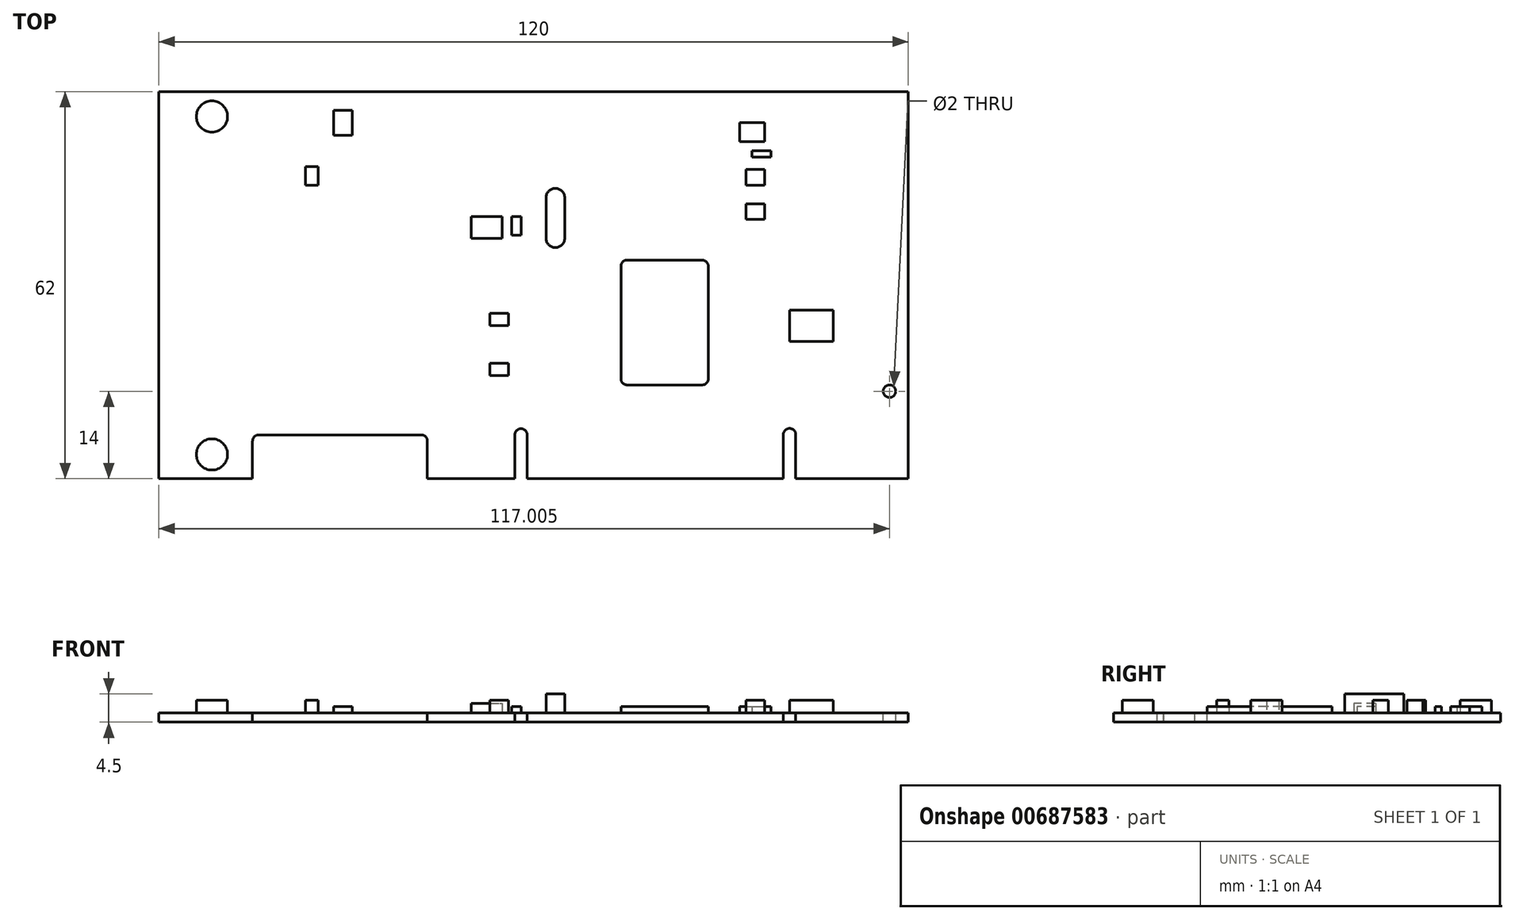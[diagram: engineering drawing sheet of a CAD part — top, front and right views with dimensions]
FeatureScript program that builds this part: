
annotation { "Feature Type Name" : "Feature", "Feature Type Description" : "" }
export const myFeature = defineFeature(function(context is Context, id is Id, definition is map)
    precondition{}
    {
        {
            var Q0;
            Q0=qCreatedBy(makeId("Top.planeOp"),FACE);
            var sketch = newSketch(context, id + "F0", { "sketchPlane" : qUnion([Q0])});
            skLineSegment(sketch, "E0.bottom", {"start": v(-77.62, 37.41) * mm, "end": v(42.38, 37.41) * mm});
            skLineSegment(sketch, "E0.top", {"start": v(-77.62, -24.59) * mm, "end": v(42.38, -24.59) * mm});
            skLineSegment(sketch, "E0.left", {"start": v(-77.62, 37.41) * mm, "end": v(-77.62, -24.59) * mm});
            skLineSegment(sketch, "E0.right", {"start": v(42.38, 37.41) * mm, "end": v(42.38, -24.59) * mm});
            skSolve(sketch);
        }
        {
            var Q0;
            Q0 = qSketchRegion(id + "F0", true);
            extrude(context, id + "F1", {"entities" : qUnion([Q0]), "depth" : 1.5 * mm, "offsetDistance" : 25 * mm});
        }
        {
            var Q0;
            Q0=makeQuery(id+"F1.opExtrude","CAP_FACE",FACE,{"disambiguationData":[OSD([sQuery(id+"F0.wireOp",EDGE,"E0.bottom"),sQuery(id+"F0.wireOp",EDGE,"E0.top"),sQuery(id+"F0.wireOp",EDGE,"E0.left"),sQuery(id+"F0.wireOp",EDGE,"E0.right")])],"isStart":false});
            var sketch = newSketch(context, id + "F2", { "sketchPlane" : qUnion([Q0])});
            skLineSegment(sketch, "E1", {"start": v(-77.62, -24.59) * mm, "end": v(-62.62, -24.59) * mm});
            skLineSegment(sketch, "E2", {"start": v(-62.62, -24.59) * mm, "end": v(-34.62, -24.59) * mm});
            skLineSegment(sketch, "E3.top", {"start": v(-61.62, -17.59) * mm, "end": v(-35.62, -17.59) * mm});
            skLineSegment(sketch, "E3.left", {"start": v(-62.62, -24.59) * mm, "end": v(-62.62, -18.59) * mm});
            skLineSegment(sketch, "E3.right", {"start": v(-34.62, -24.59) * mm, "end": v(-34.62, -18.59) * mm});
            skPoint(sketch, "E4.visualSharp", {"position": v(-62.62, -17.59) * mm});
            skArc(sketch, "E4.filletArc", {"start": v(-61.62, -17.59) * mm, "mid": v(-62.32, -17.88) * mm, "end": v(-62.62, -18.59) * mm});
            skPoint(sketch, "E5.visualSharp", {"position": v(-34.62, -17.59) * mm});
            skArc(sketch, "E5.filletArc", {"start": v(-34.62, -18.59) * mm, "mid": v(-34.9, -17.88) * mm, "end": v(-35.62, -17.59) * mm});
            skSolve(sketch);
        }
        {
            var Q0;
            Q0 = qSketchRegion(id + "F2", true);
            extrude(context, id + "F3", {"entities" : qUnion([Q0]), "operationType" : NewBodyOperationType.REMOVE, "endBound" : BoundingType.THROUGH_ALL, "oppositeDirection" : true, "depth" : 25 * mm, "offsetDistance" : 25 * mm});
        }
        {
            var Q0;
            Q0=makeQuery(id+"F1.opExtrude","CAP_FACE",FACE,{"disambiguationData":[OSD([sQuery(id+"F0.wireOp",EDGE,"E0.bottom"),sQuery(id+"F0.wireOp",EDGE,"E0.top"),sQuery(id+"F0.wireOp",EDGE,"E0.left"),sQuery(id+"F0.wireOp",EDGE,"E0.right")])],"isStart":false});
            var sketch = newSketch(context, id + "F4", { "sketchPlane" : qUnion([Q0])});
            skLineSegment(sketch, "E6", {"start": v(-34.62, -24.59) * mm, "end": v(-20.62, -24.59) * mm});
            skLineSegment(sketch, "E7", {"start": v(-20.62, -24.59) * mm, "end": v(-20.62, -17.59) * mm});
            skLineSegment(sketch, "E8", {"start": v(-18.62, -24.59) * mm, "end": v(-18.62, -17.59) * mm});
            skArc(sketch, "E9", {"start": v(-18.62, -17.59) * mm, "mid": v(-19.62, -16.59) * mm, "end": v(-20.62, -17.59) * mm});
            skPoint(sketch, "E10.orphan", {"position": v(-20.62, -16.59) * mm});
            skPoint(sketch, "E11.orphan", {"position": v(-18.62, -16.59) * mm});
            skLineSegment(sketch, "E12", {"start": v(-20.62, -24.59) * mm, "end": v(-18.62, -24.59) * mm});
            skSolve(sketch);
        }
        {
            var Q0;
            Q0 = qSketchRegion(id + "F4", true);
            extrude(context, id + "F5", {"entities" : qUnion([Q0]), "operationType" : NewBodyOperationType.REMOVE, "endBound" : BoundingType.THROUGH_ALL, "oppositeDirection" : true, "depth" : 25 * mm, "offsetDistance" : 25 * mm});
        }
        {
            var Q0;
            Q0=makeQuery(id+"F1.opExtrude","CAP_FACE",FACE,{"disambiguationData":[OSD([sQuery(id+"F0.wireOp",EDGE,"E0.bottom"),sQuery(id+"F0.wireOp",EDGE,"E0.top"),sQuery(id+"F0.wireOp",EDGE,"E0.left"),sQuery(id+"F0.wireOp",EDGE,"E0.right")])],"isStart":false});
            var sketch = newSketch(context, id + "F6", { "sketchPlane" : qUnion([Q0])});
            skLineSegment(sketch, "E13", {"start": v(-18.62, -24.59) * mm, "end": v(22.38, -24.59) * mm});
            skLineSegment(sketch, "E14", {"start": v(22.38, -24.59) * mm, "end": v(22.38, -17.54) * mm});
            skLineSegment(sketch, "E15", {"start": v(24.38, -24.59) * mm, "end": v(24.38, -17.54) * mm});
            skArc(sketch, "E16", {"start": v(24.38, -17.54) * mm, "mid": v(23.38, -16.54) * mm, "end": v(22.38, -17.54) * mm});
            skPoint(sketch, "E17.orphan", {"position": v(22.38, -16.59) * mm});
            skPoint(sketch, "E18.orphan", {"position": v(24.38, -16.59) * mm});
            skLineSegment(sketch, "E19", {"start": v(22.38, -24.59) * mm, "end": v(24.38, -24.59) * mm});
            skSolve(sketch);
        }
        {
            var Q0;
            Q0 = qSketchRegion(id + "F6", true);
            extrude(context, id + "F7", {"entities" : qUnion([Q0]), "operationType" : NewBodyOperationType.REMOVE, "endBound" : BoundingType.THROUGH_ALL, "oppositeDirection" : true, "depth" : 25 * mm, "offsetDistance" : 25 * mm});
        }
        {
            var Q0;
            Q0=makeQuery(id+"F1.opExtrude","CAP_FACE",FACE,{"disambiguationData":[OSD([sQuery(id+"F0.wireOp",EDGE,"E0.bottom"),sQuery(id+"F0.wireOp",EDGE,"E0.top"),sQuery(id+"F0.wireOp",EDGE,"E0.left"),sQuery(id+"F0.wireOp",EDGE,"E0.right")])],"isStart":false});
            var sketch = newSketch(context, id + "F8", { "sketchPlane" : qUnion([Q0])});
            skCircle(sketch, "E20", {"center": v(39.38, -10.59) * mm, "radius": 1 * mm});
            skSolve(sketch);
        }
        {
            var Q0;
            Q0 = qSketchRegion(id + "F8", true);
            extrude(context, id + "F9", {"entities" : qUnion([Q0]), "operationType" : NewBodyOperationType.REMOVE, "endBound" : BoundingType.THROUGH_ALL, "oppositeDirection" : true, "depth" : 25 * mm, "offsetDistance" : 25 * mm});
        }
        {
            var Q0;
            Q0=makeQuery(id+"F1.opExtrude","CAP_FACE",FACE,{"disambiguationData":[OSD([sQuery(id+"F0.wireOp",EDGE,"E0.bottom"),sQuery(id+"F0.wireOp",EDGE,"E0.top"),sQuery(id+"F0.wireOp",EDGE,"E0.left"),sQuery(id+"F0.wireOp",EDGE,"E0.right")])],"isStart":false});
            var sketch = newSketch(context, id + "F10", { "sketchPlane" : qUnion([Q0])});
            skLineSegment(sketch, "E21.bottom", {"start": v(23.38, 2.41) * mm, "end": v(30.38, 2.41) * mm});
            skLineSegment(sketch, "E21.top", {"start": v(23.38, -2.59) * mm, "end": v(30.38, -2.59) * mm});
            skLineSegment(sketch, "E21.left", {"start": v(23.38, 2.41) * mm, "end": v(23.38, -2.59) * mm});
            skLineSegment(sketch, "E21.right", {"start": v(30.38, 2.41) * mm, "end": v(30.38, -2.59) * mm});
            skSolve(sketch);
        }
        {
            var Q0;
            Q0 = qSketchRegion(id + "F10", true);
            extrude(context, id + "F11", {"entities" : qUnion([Q0]), "operationType" : NewBodyOperationType.ADD, "depth" : 2 * mm, "offsetDistance" : 25 * mm});
        }
        {
            var Q0;
            Q0=makeQuery(id+"F1.opExtrude","CAP_FACE",FACE,{"disambiguationData":[OSD([sQuery(id+"F0.wireOp",EDGE,"E0.bottom"),sQuery(id+"F0.wireOp",EDGE,"E0.top"),sQuery(id+"F0.wireOp",EDGE,"E0.left"),sQuery(id+"F0.wireOp",EDGE,"E0.right")])],"isStart":false});
            var sketch = newSketch(context, id + "F12", { "sketchPlane" : qUnion([Q0])});
            skLineSegment(sketch, "E22.bottom", {"start": v(-2.62, 10.41) * mm, "end": v(9.38, 10.41) * mm});
            skLineSegment(sketch, "E22.top", {"start": v(-2.62, -9.59) * mm, "end": v(9.38, -9.59) * mm});
            skLineSegment(sketch, "E22.left", {"start": v(-3.62, 9.41) * mm, "end": v(-3.62, -8.59) * mm});
            skLineSegment(sketch, "E22.right", {"start": v(10.38, 9.41) * mm, "end": v(10.38, -8.59) * mm});
            skPoint(sketch, "E23.visualSharp", {"position": v(-3.62, 10.41) * mm});
            skArc(sketch, "E23.filletArc", {"start": v(-2.62, 10.41) * mm, "mid": v(-3.32, 10.12) * mm, "end": v(-3.62, 9.41) * mm});
            skPoint(sketch, "E24.visualSharp", {"position": v(10.38, 10.41) * mm});
            skArc(sketch, "E24.filletArc", {"start": v(10.38, 9.41) * mm, "mid": v(10.1, 10.12) * mm, "end": v(9.38, 10.41) * mm});
            skPoint(sketch, "E25.visualSharp", {"position": v(-3.62, -9.59) * mm});
            skArc(sketch, "E25.filletArc", {"start": v(-3.62, -8.59) * mm, "mid": v(-3.32, -9.3) * mm, "end": v(-2.62, -9.59) * mm});
            skPoint(sketch, "E26.visualSharp", {"position": v(10.38, -9.59) * mm});
            skArc(sketch, "E26.filletArc", {"start": v(9.38, -9.59) * mm, "mid": v(10.1, -9.3) * mm, "end": v(10.38, -8.59) * mm});
            skSolve(sketch);
        }
        {
            var Q0;
            Q0 = qSketchRegion(id + "F12", true);
            extrude(context, id + "F13", {"entities" : qUnion([Q0]), "operationType" : NewBodyOperationType.ADD, "depth" : 1 * mm, "offsetDistance" : 25 * mm});
        }
        {
            var Q0;
            Q0=makeQuery(id+"F1.opExtrude","CAP_FACE",FACE,{"disambiguationData":[OSD([sQuery(id+"F0.wireOp",EDGE,"E0.bottom"),sQuery(id+"F0.wireOp",EDGE,"E0.top"),sQuery(id+"F0.wireOp",EDGE,"E0.left"),sQuery(id+"F0.wireOp",EDGE,"E0.right")])],"isStart":false});
            var sketch = newSketch(context, id + "F14", { "sketchPlane" : qUnion([Q0])});
            skLineSegment(sketch, "E27.bottom", {"start": v(16.38, 19.41) * mm, "end": v(19.38, 19.41) * mm});
            skLineSegment(sketch, "E27.top", {"start": v(16.38, 16.91) * mm, "end": v(19.38, 16.91) * mm});
            skLineSegment(sketch, "E27.left", {"start": v(16.38, 19.41) * mm, "end": v(16.38, 16.91) * mm});
            skLineSegment(sketch, "E27.right", {"start": v(19.38, 19.41) * mm, "end": v(19.38, 16.91) * mm});
            skSolve(sketch);
        }
        {
            var Q0;
            Q0 = qSketchRegion(id + "F14", true);
            extrude(context, id + "F15", {"entities" : qUnion([Q0]), "operationType" : NewBodyOperationType.ADD, "depth" : 2 * mm, "offsetDistance" : 25 * mm});
        }
        {
            var Q0;
            Q0=makeQuery(id+"F1.opExtrude","CAP_FACE",FACE,{"disambiguationData":[OSD([sQuery(id+"F0.wireOp",EDGE,"E0.bottom"),sQuery(id+"F0.wireOp",EDGE,"E0.top"),sQuery(id+"F0.wireOp",EDGE,"E0.left"),sQuery(id+"F0.wireOp",EDGE,"E0.right")])],"isStart":false});
            var sketch = newSketch(context, id + "F16", { "sketchPlane" : qUnion([Q0])});
            skLineSegment(sketch, "E28.bottom", {"start": v(19.38, 22.41) * mm, "end": v(16.38, 22.41) * mm});
            skLineSegment(sketch, "E28.top", {"start": v(19.38, 24.91) * mm, "end": v(16.38, 24.91) * mm});
            skLineSegment(sketch, "E28.left", {"start": v(19.38, 22.41) * mm, "end": v(19.38, 24.91) * mm});
            skLineSegment(sketch, "E28.right", {"start": v(16.38, 22.41) * mm, "end": v(16.38, 24.91) * mm});
            skSolve(sketch);
        }
        {
            var Q0;
            Q0 = qSketchRegion(id + "F16", true);
            extrude(context, id + "F17", {"entities" : qUnion([Q0]), "operationType" : NewBodyOperationType.ADD, "depth" : 2 * mm, "offsetDistance" : 25 * mm});
        }
        {
            var Q0;
            Q0=makeQuery(id+"F1.opExtrude","CAP_FACE",FACE,{"disambiguationData":[OSD([sQuery(id+"F0.wireOp",EDGE,"E0.bottom"),sQuery(id+"F0.wireOp",EDGE,"E0.top"),sQuery(id+"F0.wireOp",EDGE,"E0.left"),sQuery(id+"F0.wireOp",EDGE,"E0.right")])],"isStart":false});
            var sketch = newSketch(context, id + "F18", { "sketchPlane" : qUnion([Q0])});
            skLineSegment(sketch, "E29.bottom", {"start": v(17.38, 27.91) * mm, "end": v(20.38, 27.91) * mm});
            skLineSegment(sketch, "E29.top", {"start": v(17.38, 26.91) * mm, "end": v(20.38, 26.91) * mm});
            skLineSegment(sketch, "E29.left", {"start": v(17.38, 27.91) * mm, "end": v(17.38, 26.91) * mm});
            skLineSegment(sketch, "E29.right", {"start": v(20.38, 27.91) * mm, "end": v(20.38, 26.91) * mm});
            skSolve(sketch);
        }
        {
            var Q0;
            Q0 = qSketchRegion(id + "F18", true);
            extrude(context, id + "F19", {"entities" : qUnion([Q0]), "operationType" : NewBodyOperationType.ADD, "depth" : 1 * mm, "offsetDistance" : 25 * mm});
        }
        {
            var Q0;
            Q0=makeQuery(id+"F1.opExtrude","CAP_FACE",FACE,{"disambiguationData":[OSD([sQuery(id+"F0.wireOp",EDGE,"E0.bottom"),sQuery(id+"F0.wireOp",EDGE,"E0.top"),sQuery(id+"F0.wireOp",EDGE,"E0.left"),sQuery(id+"F0.wireOp",EDGE,"E0.right")])],"isStart":false});
            var sketch = newSketch(context, id + "F20", { "sketchPlane" : qUnion([Q0])});
            skLineSegment(sketch, "E30.bottom", {"start": v(15.38, 32.41) * mm, "end": v(19.38, 32.41) * mm});
            skLineSegment(sketch, "E30.top", {"start": v(15.38, 29.41) * mm, "end": v(19.38, 29.41) * mm});
            skLineSegment(sketch, "E30.left", {"start": v(15.38, 32.41) * mm, "end": v(15.38, 29.41) * mm});
            skLineSegment(sketch, "E30.right", {"start": v(19.38, 32.41) * mm, "end": v(19.38, 29.41) * mm});
            skSolve(sketch);
        }
        {
            var Q0;
            Q0 = qSketchRegion(id + "F20", true);
            extrude(context, id + "F21", {"entities" : qUnion([Q0]), "operationType" : NewBodyOperationType.ADD, "depth" : 1 * mm, "offsetDistance" : 25 * mm});
        }
        {
            var Q0;
            Q0=makeQuery(id+"F1.opExtrude","CAP_FACE",FACE,{"disambiguationData":[OSD([sQuery(id+"F0.wireOp",EDGE,"E0.bottom"),sQuery(id+"F0.wireOp",EDGE,"E0.top"),sQuery(id+"F0.wireOp",EDGE,"E0.left"),sQuery(id+"F0.wireOp",EDGE,"E0.right")])],"isStart":false});
            var sketch = newSketch(context, id + "F22", { "sketchPlane" : qUnion([Q0])});
            skLineSegment(sketch, "E31.bottom", {"start": v(-14.12, 21.91) * mm, "end": v(-14.12, 21.91) * mm});
            skLineSegment(sketch, "E31.top", {"start": v(-14.12, 12.41) * mm, "end": v(-14.12, 12.41) * mm});
            skLineSegment(sketch, "E31.left", {"start": v(-15.62, 20.41) * mm, "end": v(-15.62, 13.91) * mm});
            skLineSegment(sketch, "E31.right", {"start": v(-12.62, 20.41) * mm, "end": v(-12.62, 13.91) * mm});
            skPoint(sketch, "E32.visualSharp", {"position": v(-15.62, 21.91) * mm});
            skArc(sketch, "E32.filletArc", {"start": v(-14.12, 21.91) * mm, "mid": v(-15.18, 21.47) * mm, "end": v(-15.62, 20.41) * mm});
            skPoint(sketch, "E33.visualSharp", {"position": v(-12.62, 21.91) * mm});
            skArc(sketch, "E33.filletArc", {"start": v(-12.62, 20.41) * mm, "mid": v(-13.05, 21.47) * mm, "end": v(-14.12, 21.91) * mm});
            skPoint(sketch, "E34.visualSharp", {"position": v(-15.62, 12.41) * mm});
            skArc(sketch, "E34.filletArc", {"start": v(-15.62, 13.91) * mm, "mid": v(-15.18, 12.85) * mm, "end": v(-14.12, 12.41) * mm});
            skPoint(sketch, "E35.visualSharp", {"position": v(-12.62, 12.41) * mm});
            skArc(sketch, "E35.filletArc", {"start": v(-14.12, 12.41) * mm, "mid": v(-13.05, 12.85) * mm, "end": v(-12.62, 13.91) * mm});
            skSolve(sketch);
        }
        {
            var Q0;
            Q0 = qSketchRegion(id + "F22", true);
            extrude(context, id + "F23", {"entities" : qUnion([Q0]), "operationType" : NewBodyOperationType.ADD, "depth" : 3 * mm, "offsetDistance" : 25 * mm});
        }
        {
            var Q0;
            Q0=makeQuery(id+"F1.opExtrude","CAP_FACE",FACE,{"disambiguationData":[OSD([sQuery(id+"F0.wireOp",EDGE,"E0.bottom"),sQuery(id+"F0.wireOp",EDGE,"E0.top"),sQuery(id+"F0.wireOp",EDGE,"E0.left"),sQuery(id+"F0.wireOp",EDGE,"E0.right")])],"isStart":false});
            var sketch = newSketch(context, id + "F24", { "sketchPlane" : qUnion([Q0])});
            skLineSegment(sketch, "E36.bottom", {"start": v(-21.12, 17.41) * mm, "end": v(-19.62, 17.41) * mm});
            skLineSegment(sketch, "E36.top", {"start": v(-21.12, 14.41) * mm, "end": v(-19.62, 14.41) * mm});
            skLineSegment(sketch, "E36.left", {"start": v(-21.12, 17.41) * mm, "end": v(-21.12, 14.41) * mm});
            skLineSegment(sketch, "E36.right", {"start": v(-19.62, 17.41) * mm, "end": v(-19.62, 14.41) * mm});
            skSolve(sketch);
        }
        {
            var Q0;
            Q0 = qSketchRegion(id + "F24", true);
            extrude(context, id + "F25", {"entities" : qUnion([Q0]), "operationType" : NewBodyOperationType.ADD, "depth" : 1 * mm, "offsetDistance" : 25 * mm});
        }
        {
            var Q0;
            Q0=makeQuery(id+"F1.opExtrude","CAP_FACE",FACE,{"disambiguationData":[OSD([sQuery(id+"F0.wireOp",EDGE,"E0.bottom"),sQuery(id+"F0.wireOp",EDGE,"E0.top"),sQuery(id+"F0.wireOp",EDGE,"E0.left"),sQuery(id+"F0.wireOp",EDGE,"E0.right")])],"isStart":false});
            var sketch = newSketch(context, id + "F26", { "sketchPlane" : qUnion([Q0])});
            skLineSegment(sketch, "E37.bottom", {"start": v(-27.62, 17.41) * mm, "end": v(-22.62, 17.41) * mm});
            skLineSegment(sketch, "E37.top", {"start": v(-27.62, 13.91) * mm, "end": v(-22.62, 13.91) * mm});
            skLineSegment(sketch, "E37.left", {"start": v(-27.62, 17.41) * mm, "end": v(-27.62, 13.91) * mm});
            skLineSegment(sketch, "E37.right", {"start": v(-22.62, 17.41) * mm, "end": v(-22.62, 13.91) * mm});
            skSolve(sketch);
        }
        {
            var Q0;
            Q0 = qSketchRegion(id + "F26", true);
            extrude(context, id + "F27", {"entities" : qUnion([Q0]), "operationType" : NewBodyOperationType.ADD, "depth" : 1.5 * mm, "offsetDistance" : 25 * mm});
        }
        {
            var Q0;
            Q0=makeQuery(id+"F1.opExtrude","CAP_FACE",FACE,{"disambiguationData":[OSD([sQuery(id+"F0.wireOp",EDGE,"E0.bottom"),sQuery(id+"F0.wireOp",EDGE,"E0.top"),sQuery(id+"F0.wireOp",EDGE,"E0.left"),sQuery(id+"F0.wireOp",EDGE,"E0.right")])],"isStart":false});
            var sketch = newSketch(context, id + "F28", { "sketchPlane" : qUnion([Q0])});
            skLineSegment(sketch, "E38.bottom", {"start": v(-24.62, 1.91) * mm, "end": v(-21.62, 1.91) * mm});
            skLineSegment(sketch, "E38.top", {"start": v(-24.62, -0.09) * mm, "end": v(-21.62, -0.09) * mm});
            skLineSegment(sketch, "E38.left", {"start": v(-24.62, 1.91) * mm, "end": v(-24.62, -0.09) * mm});
            skLineSegment(sketch, "E38.right", {"start": v(-21.62, 1.91) * mm, "end": v(-21.62, -0.09) * mm});
            skSolve(sketch);
        }
        {
            var Q0;
            Q0 = qSketchRegion(id + "F28", true);
            extrude(context, id + "F29", {"entities" : qUnion([Q0]), "operationType" : NewBodyOperationType.ADD, "depth" : 2 * mm, "offsetDistance" : 25 * mm});
        }
        {
            var Q0;
            Q0=makeQuery(id+"F1.opExtrude","CAP_FACE",FACE,{"disambiguationData":[OSD([sQuery(id+"F0.wireOp",EDGE,"E0.bottom"),sQuery(id+"F0.wireOp",EDGE,"E0.top"),sQuery(id+"F0.wireOp",EDGE,"E0.left"),sQuery(id+"F0.wireOp",EDGE,"E0.right")])],"isStart":false});
            var sketch = newSketch(context, id + "F30", { "sketchPlane" : qUnion([Q0])});
            skLineSegment(sketch, "E39.bottom", {"start": v(-21.62, -6.09) * mm, "end": v(-24.62, -6.09) * mm});
            skLineSegment(sketch, "E39.top", {"start": v(-21.62, -8.09) * mm, "end": v(-24.62, -8.09) * mm});
            skLineSegment(sketch, "E39.left", {"start": v(-21.62, -6.09) * mm, "end": v(-21.62, -8.09) * mm});
            skLineSegment(sketch, "E39.right", {"start": v(-24.62, -6.09) * mm, "end": v(-24.62, -8.09) * mm});
            skSolve(sketch);
        }
        {
            var Q0;
            Q0 = qSketchRegion(id + "F30", true);
            extrude(context, id + "F31", {"entities" : qUnion([Q0]), "operationType" : NewBodyOperationType.ADD, "depth" : 2 * mm, "offsetDistance" : 25 * mm});
        }
        {
            var Q0;
            Q0=makeQuery(id+"F1.opExtrude","CAP_FACE",FACE,{"disambiguationData":[OSD([sQuery(id+"F0.wireOp",EDGE,"E0.bottom"),sQuery(id+"F0.wireOp",EDGE,"E0.top"),sQuery(id+"F0.wireOp",EDGE,"E0.left"),sQuery(id+"F0.wireOp",EDGE,"E0.right")])],"isStart":false});
            var sketch = newSketch(context, id + "F32", { "sketchPlane" : qUnion([Q0])});
            skCircle(sketch, "E40", {"center": v(-69.12, 33.41) * mm, "radius": 2.5 * mm});
            skSolve(sketch);
        }
        {
            var Q0;
            Q0 = qSketchRegion(id + "F32", true);
            extrude(context, id + "F33", {"entities" : qUnion([Q0]), "operationType" : NewBodyOperationType.ADD, "depth" : 2 * mm, "offsetDistance" : 25 * mm});
        }
        {
            var Q0;
            Q0=makeQuery(id+"F1.opExtrude","CAP_FACE",FACE,{"disambiguationData":[OSD([sQuery(id+"F0.wireOp",EDGE,"E0.bottom"),sQuery(id+"F0.wireOp",EDGE,"E0.top"),sQuery(id+"F0.wireOp",EDGE,"E0.left"),sQuery(id+"F0.wireOp",EDGE,"E0.right")])],"isStart":false});
            var sketch = newSketch(context, id + "F34", { "sketchPlane" : qUnion([Q0])});
            skCircle(sketch, "E41", {"center": v(-69.12, -20.72) * mm, "radius": 2.5 * mm});
            skSolve(sketch);
        }
        {
            var Q0;
            Q0 = qSketchRegion(id + "F34", true);
            extrude(context, id + "F35", {"entities" : qUnion([Q0]), "operationType" : NewBodyOperationType.ADD, "depth" : 2 * mm, "offsetDistance" : 25 * mm});
        }
        {
            var Q0;
            Q0=makeQuery(id+"F1.opExtrude","CAP_FACE",FACE,{"disambiguationData":[OSD([sQuery(id+"F0.wireOp",EDGE,"E0.bottom"),sQuery(id+"F0.wireOp",EDGE,"E0.top"),sQuery(id+"F0.wireOp",EDGE,"E0.left"),sQuery(id+"F0.wireOp",EDGE,"E0.right")])],"isStart":false});
            var sketch = newSketch(context, id + "F36", { "sketchPlane" : qUnion([Q0])});
            skLineSegment(sketch, "E42.bottom", {"start": v(-49.62, 34.41) * mm, "end": v(-46.62, 34.41) * mm});
            skLineSegment(sketch, "E42.top", {"start": v(-49.62, 30.41) * mm, "end": v(-46.62, 30.41) * mm});
            skLineSegment(sketch, "E42.left", {"start": v(-49.62, 34.41) * mm, "end": v(-49.62, 30.41) * mm});
            skLineSegment(sketch, "E42.right", {"start": v(-46.62, 34.41) * mm, "end": v(-46.62, 30.41) * mm});
            skSolve(sketch);
        }
        {
            var Q0;
            Q0 = qSketchRegion(id + "F36", true);
            extrude(context, id + "F37", {"entities" : qUnion([Q0]), "operationType" : NewBodyOperationType.ADD, "depth" : 1 * mm, "offsetDistance" : 25 * mm});
        }
        {
            var Q0;
            Q0=makeQuery(id+"F1.opExtrude","CAP_FACE",FACE,{"disambiguationData":[OSD([sQuery(id+"F0.wireOp",EDGE,"E0.bottom"),sQuery(id+"F0.wireOp",EDGE,"E0.top"),sQuery(id+"F0.wireOp",EDGE,"E0.left"),sQuery(id+"F0.wireOp",EDGE,"E0.right")])],"isStart":false});
            var sketch = newSketch(context, id + "F38", { "sketchPlane" : qUnion([Q0])});
            skLineSegment(sketch, "E43.bottom", {"start": v(-54.12, 25.41) * mm, "end": v(-52.12, 25.41) * mm});
            skLineSegment(sketch, "E43.top", {"start": v(-54.12, 22.41) * mm, "end": v(-52.12, 22.41) * mm});
            skLineSegment(sketch, "E43.left", {"start": v(-54.12, 25.41) * mm, "end": v(-54.12, 22.41) * mm});
            skLineSegment(sketch, "E43.right", {"start": v(-52.12, 25.41) * mm, "end": v(-52.12, 22.41) * mm});
            skSolve(sketch);
        }
        {
            var Q0;
            Q0 = qSketchRegion(id + "F38", true);
            extrude(context, id + "F39", {"entities" : qUnion([Q0]), "operationType" : NewBodyOperationType.ADD, "depth" : 2 * mm, "offsetDistance" : 25 * mm});
        }
    });
